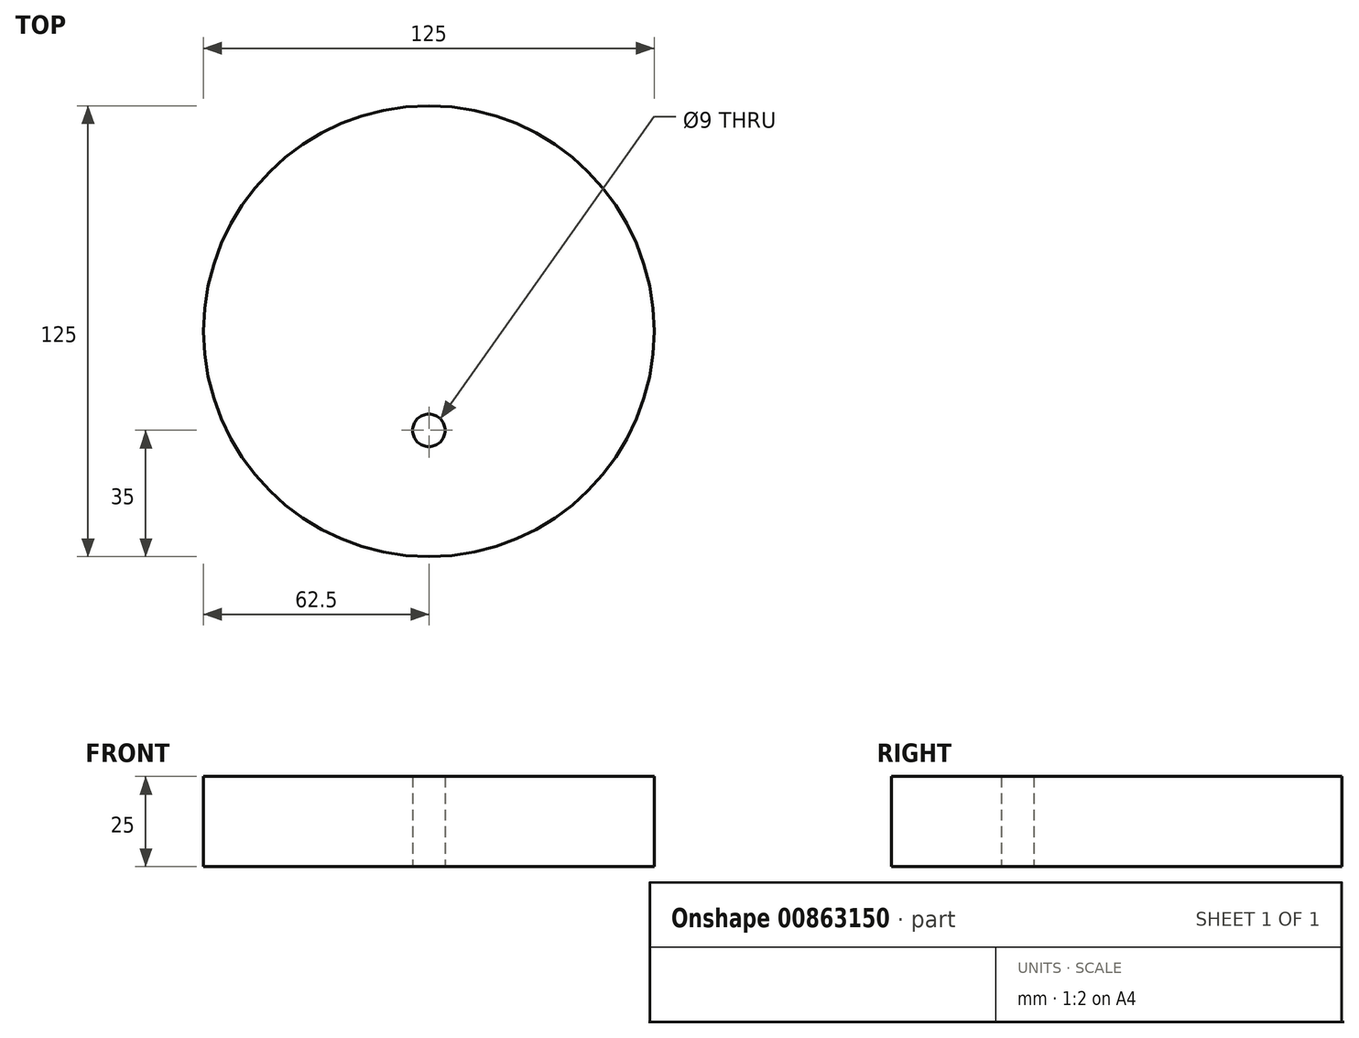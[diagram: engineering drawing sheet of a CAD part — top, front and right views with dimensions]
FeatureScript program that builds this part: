
annotation { "Feature Type Name" : "Feature", "Feature Type Description" : "" }
export const myFeature = defineFeature(function(context is Context, id is Id, definition is map)
    precondition{}
    {
        {
            var Q0;
            Q0=qCreatedBy(makeId("Top.planeOp"),FACE);
            var sketch = newSketch(context, id + "F0", { "sketchPlane" : qUnion([Q0])});
            skCircle(sketch, "E0", {"center": v(0, 0) * mm, "radius": 62.5 * mm});
            skCircle(sketch, "E1", {"center": v(0, 0) * mm, "radius": 27.5 * mm, "construction": true});
            skCircle(sketch, "E2", {"center": v(0, -27.5) * mm, "radius": 4.5 * mm});
            skSolve(sketch);
        }
        {
            var Q0;
            Q0 = qSketchRegion(id + "F0", true);
            extrude(context, id + "F1", {"entities" : qUnion([Q0]), "depth" : 25 * mm, "offsetDistance" : 25 * mm});
        }
    });
